# Revit family: Hager-Gamma-IP30-syst-SE-en
name_source: partatom
category: Electrical Equipment
units: mm (PartAtom-declared; Revit-internal decimal feet)

## family parameters
Cut with Voids When Loaded = No
Host = Face
Panel Configuration = Two Columns, Circuits Across
Part Type = Panelboard
Room Calculation Point = No
Round Connector Dimension = Use Diameter
Shared = No

## types (18) — shared parameters
EF000003 - Mounting method = EV000384 - Surface mounted (plaster)
EF000339 - Type of cover = EV001012 - Cover
EF001062 - EMC-version = No
EF001088 - Extension possible = Yes
EF004462 - Type of closure = EV000154 - Other
EF005474 - Degree of protection (IP) = EV006410 - IP30
EF006244 - Transparent cover/door = No
EF006306 - With lock = No
EF009212 - Cover model = EV009916 - With notch
HG000001 - Number of columns = 1
HG000003 - Range = Gamma
HG000005 - Thickness = 3 mm  [stored 0.00984252 ft]
HG000006 - Flush mounted = No
HG000009 - Double swing door = No
HG000010 - Asymmetric doors = No
HG000011 - Empty rows from bottom = No
HG000017 - Distance between poles = 18 mm  [stored 0.0590551 ft]
Manufacturer = Hager
Type Comments = Gamma
zero-valued in all types: Default Elevation, EF000218 - Built-in depth, EF000332 - Built-in height, EF000846 - Built-in width, HG000007 - Number of empty columns, HG000008 - Number of empty rows

## per-type parameters (varying)
| type | EF000007 - Colour | EF000008 - Width | EF000040 - Height | EF000049 - Depth | EF000116 - RAL-number | EF000118 - With mounting plate | EF000266 - Number of rows | EF001131 - Internal depth | EF001134 - DIN-rail | EF001596 - Material housing | EF002950 - Width in number of modular spacings | EF015776 - Earthing terminal block | EF015777 - Neutral terminal block | EF015941 - Signal passing door | HG000002 - With door or cover | HG000004 - Manufacturer reference | Model |
| Surface mounted IP30 W250 H250 D103 13 Modular spacings - GD113S | EV000202 - White | 250 mm  [stored 0.82021 ft] | 250 mm  [stored 0.82021 ft] | 103 mm  [stored 0.337927 ft] | 9010 | Yes | 1 | 103 mm  [stored 0.337927 ft] | Yes | EV000139 - Plastic | 13 | No | No | No | No | GD113S | GD113S |
| Surface mounted IP30 W250 H250 D130 13 Modular spacings - GD113N | EV000202 - White | 250 mm  [stored 0.82021 ft] | 250 mm  [stored 0.82021 ft] | 130 mm  [stored 0.426509 ft] | 9010 | Yes | 1 | 130 mm  [stored 0.426509 ft] | Yes | EV000179 - Steel | 13 | Yes | Yes | No | Yes | GD113N | GD113N |
| Surface mounted IP30 W250 H375 D103 13 Modular spacings - GD213S | EV000202 - White | 250 mm  [stored 0.82021 ft] | 375 mm  [stored 1.23031 ft] | 103 mm  [stored 0.337927 ft] | 9010 | Yes | 2 | 103 mm  [stored 0.337927 ft] | Yes | EV000139 - Plastic | 13 | No | No | No | No | GD213S | GD213S |
| Surface mounted IP30 W250 H375 D130 13 Modular spacings - GD213N | EV000202 - White | 250 mm  [stored 0.82021 ft] | 375 mm  [stored 1.23031 ft] | 130 mm  [stored 0.426509 ft] | 9010 | Yes | 2 | 130 mm  [stored 0.426509 ft] | Yes | EV000179 - Steel | 13 | Yes | Yes | No | Yes | GD213N | GD213N |
| Surface mounted IP30 W250 H500 D103 13 Modular spacings - GD313S | EV000202 - White | 250 mm  [stored 0.82021 ft] | 500 mm  [stored 1.64042 ft] | 103 mm  [stored 0.337927 ft] | 9010 | Yes | 3 | 103 mm  [stored 0.337927 ft] | Yes | EV000139 - Plastic | 13 | No | No | No | No | GD313S | GD313S |
| Surface mounted IP30 W250 H500 D130 13 Modular spacings - GD313N | EV000202 - White | 250 mm  [stored 0.82021 ft] | 500 mm  [stored 1.64042 ft] | 130 mm  [stored 0.426509 ft] | 9010 | Yes | 3 | 130 mm  [stored 0.426509 ft] | Yes | EV000179 - Steel | 13 | Yes | Yes | No | Yes | GD313N | GD313N |
| Surface mounted IP30 W250 H625 D103 13 Modular spacings - GD413S | EV000202 - White | 250 mm  [stored 0.82021 ft] | 625 mm  [stored 2.05052 ft] | 103 mm  [stored 0.337927 ft] | 9010 | Yes | 4 | 103 mm  [stored 0.337927 ft] | Yes | EV000139 - Plastic | 13 | No | No | No | No | GD413S | GD413S |
| Surface mounted IP30 W250 H625 D130 13 Modular spacings - GD413N | EV000202 - White | 250 mm  [stored 0.82021 ft] | 625 mm  [stored 2.05052 ft] | 130 mm  [stored 0.426509 ft] | 9010 | Yes | 4 | 130 mm  [stored 0.426509 ft] | Yes | EV000179 - Steel | 13 | Yes | Yes | No | Yes | GD413N | GD413N |
| Surface mounted IP30 W355 H250 D103 18 Modular spacings - GD118S | EV000202 - White | 355 mm | 250 mm  [stored 0.82021 ft] | 103 mm  [stored 0.337927 ft] | 9010 | Yes | 1 | 103 mm  [stored 0.337927 ft] | Yes | EV000139 - Plastic | 18 | No | No | No | No | GD118S | GD118S |
| Surface mounted IP30 W355 H250 D130 18 Modular spacings - GD118N | EV000202 - White | 355 mm | 250 mm  [stored 0.82021 ft] | 130 mm  [stored 0.426509 ft] | 9010 | Yes | 1 | 130 mm  [stored 0.426509 ft] | Yes | EV000179 - Steel | 18 | Yes | Yes | No | Yes | GD118N | GD118N |
| Surface mounted IP30 W355 H375 D103 18 Modular spacings - GD218S | EV000202 - White | 355 mm | 375 mm  [stored 1.23031 ft] | 103 mm  [stored 0.337927 ft] | 9010 | Yes | 2 | 103 mm  [stored 0.337927 ft] | Yes | EV000139 - Plastic | 18 | No | No | No | No | GD218S | GD218S |
| Surface mounted IP30 W355 H375 D130 18 Modular spacings - GD218N | EV000202 - White | 355 mm | 375 mm  [stored 1.23031 ft] | 130 mm  [stored 0.426509 ft] | 9010 | Yes | 2 | 130 mm  [stored 0.426509 ft] | Yes | EV000179 - Steel | 18 | Yes | Yes | No | Yes | GD218N | GD218N |
| Surface mounted IP30 W355 H500 D103 18 Modular spacings - GD318S | EV000202 - White | 355 mm | 500 mm  [stored 1.64042 ft] | 103 mm  [stored 0.337927 ft] | 9010 | Yes | 3 | 103 mm  [stored 0.337927 ft] | Yes | EV000139 - Plastic | 18 | No | No | No | No | GD318S | GD318S |
| Surface mounted IP30 W355 H500 D130 18 Modular spacings - GD318N | EV000202 - White | 355 mm | 500 mm  [stored 1.64042 ft] | 130 mm  [stored 0.426509 ft] | 9010 | Yes | 3 | 130 mm  [stored 0.426509 ft] | Yes | EV000179 - Steel | 18 | Yes | Yes | No | Yes | GD318N | GD318N |
| Surface mounted IP30 W355 H625 D103 18 Modular spacings - GD418S | EV000202 - White | 355 mm | 625 mm  [stored 2.05052 ft] | 103 mm  [stored 0.337927 ft] | 9010 | Yes | 4 | 103 mm  [stored 0.337927 ft] | Yes | EV000139 - Plastic | 18 | No | No | No | No | GD418S | GD418S |
| Surface mounted IP30 W355 H625 D130 18 Modular spacings - GD418N | EV000202 - White | 355 mm | 625 mm  [stored 2.05052 ft] | 130 mm  [stored 0.426509 ft] | 9010 | Yes | 4 | 130 mm  [stored 0.426509 ft] | Yes | EV000179 - Steel | 18 | Yes | Yes | No | Yes | GD418N | GD418N |
| Surface mounted IP30 W500 H250 D130 26 Modular spacings - GD126N | EV000270 - Grey | 500 mm  [stored 1.64042 ft] | 250 mm  [stored 0.82021 ft] | 130 mm  [stored 0.426509 ft] | 7035 | No | 1 | 0 mm  [stored 0 ft] | No | EV000179 - Steel | 26 | Yes | Yes | Yes | Yes | GD126N | GD126N |
| Surface mounted IP30 W500 H375 D130 26 Modular spacings - GD226N | EV000270 - Grey | 500 mm  [stored 1.64042 ft] | 375 mm  [stored 1.23031 ft] | 130 mm  [stored 0.426509 ft] | 7035 | No | 2 | 10 mm  [stored 0.0328084 ft] | No | EV000179 - Steel | 26 | Yes | Yes | Yes | Yes | GD226N | GD226N |

note: [stored X ft] marks values corroborated as IEEE doubles in the binary element streams (Revit-internal decimal feet)

## geometry (parser evidence)
native form markers: Sweep x17
no freeform markers — native parametric forms only
